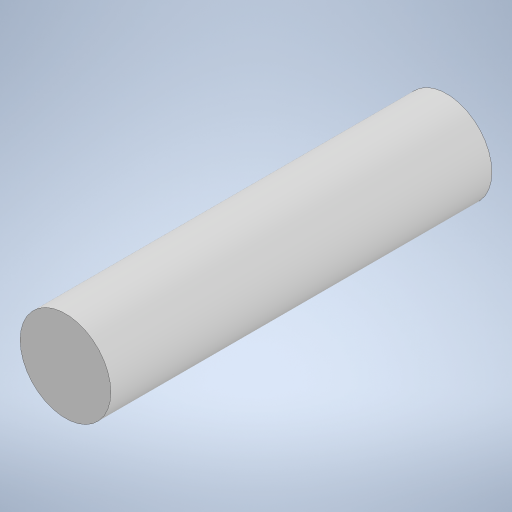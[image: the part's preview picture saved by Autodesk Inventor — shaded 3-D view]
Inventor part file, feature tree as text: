
AUTODESK INVENTOR PART (.ipt)
format: ipt  version: 2023.5 (Build 275446000, 446)  size: 230,912 bytes
history: native  units: in
note: dims shown in document units (in); Inventor stores cm internally (conversion verified against a paired STEP export)
features: extrude x1, sketch x1
ambient origin geometry x8: Origin, YZ Plane, XZ Plane, XY Plane, X Axis, Y Axis, Z Axis, Center Point
bodies: Solid1 (feature_tree)
feature tree (2):
  extrude  "Extrusion1"  Depth=0.4134in TaperAngle=0.0deg
  sketch  "Sketch1"  dims[d0=0.0984in d1=0.4134in d2=0.0in]
